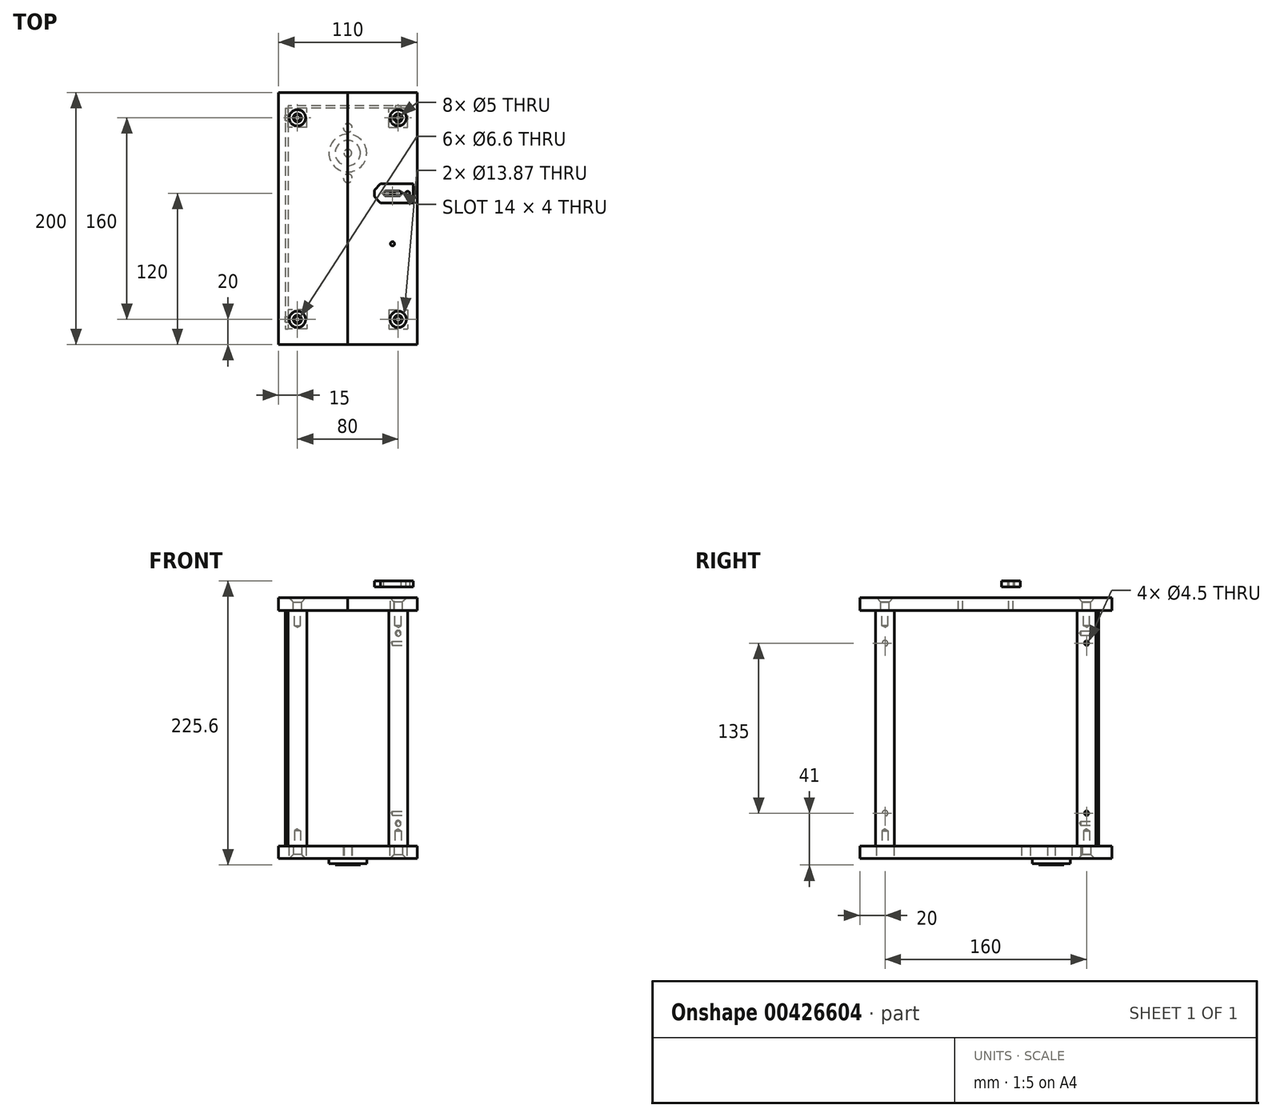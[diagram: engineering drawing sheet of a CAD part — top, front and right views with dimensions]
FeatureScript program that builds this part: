
annotation { "Feature Type Name" : "Feature", "Feature Type Description" : "" }
export const myFeature = defineFeature(function(context is Context, id is Id, definition is map)
    precondition{}
    {
        {
            var Q0;
            Q0=qCreatedBy(makeId("Top.planeOp"),FACE);
            cPlane(context, id + "F0", {"entities" : qUnion([Q0]), "cplaneType" : CPlaneType.OFFSET, "offset" : 197 * mm, "width" : 150 * mm, "height" : 150 * mm});
        }
        {
            var Q0;
            Q0=qCreatedBy(makeId("Front.planeOp"),FACE);
            var sketch = newSketch(context, id + "F1", { "sketchPlane" : qUnion([Q0])});
            skLineSegment(sketch, "E0", {"start": v(0, 0) * mm, "end": v(0, 306.43) * mm});
            skSolve(sketch);
        }
        {
            var Q0;
            Q0=qCreatedBy(makeId("Top.planeOp"),FACE);
            var sketch = newSketch(context, id + "F2", { "sketchPlane" : qUnion([Q0])});
            skCircle(sketch, "E1", {"center": v(0, 20) * mm, "radius": 3.5 * mm});
            skCircle(sketch, "E2.MirrorC", {"center": v(0, -20) * mm, "radius": 3.5 * mm});
            skPoint(sketch, "E3", {"position": v(0, 0) * mm});
            skSolve(sketch);
        }
        {
            var Q0;
            Q0=qCreatedBy(makeId("Top.planeOp"),FACE);
            var sketch = newSketch(context, id + "F3", { "sketchPlane" : qUnion([Q0])});
            skLineSegment(sketch, "E4.bottom", {"start": v(0, 48) * mm, "end": v(55, 48) * mm});
            skLineSegment(sketch, "E4.top", {"start": v(0, -152) * mm, "end": v(55, -152) * mm});
            skLineSegment(sketch, "E4.left", {"start": v(0, 48) * mm, "end": v(0, -152) * mm});
            skLineSegment(sketch, "E4.right", {"start": v(55, 48) * mm, "end": v(55, -152) * mm});
            skCircle(sketch, "E5", {"center": v(40, 28) * mm, "radius": 6.93 * mm});
            skLineSegment(sketch, "E6", {"start": v(55, -52) * mm, "end": v(0, -52) * mm, "construction": true});
            skCircle(sketch, "E7.MirrorC", {"center": v(40, -132) * mm, "radius": 6.93 * mm});
            skSolve(sketch);
        }
        {
            var Q0;
            Q0=sQuery(id+"F3.wireOp",VERTEX,"E4.right.start");
            var Q1;
            Q1=sQuery(id+"F3.wireOp",VERTEX,"E4.right.end");
            cPlane(context, id + "F4", {"entities" : qUnion([Q0, Q1]), "cplaneType" : CPlaneType.MID_PLANE, "offset" : 25 * mm, "width" : 150 * mm, "height" : 150 * mm});
        }
        {
            var Q0;
            Q0=makeQuery(id+"F3.imprint","IMPRINT",FACE,{"disambiguationData":[TD([[makeQuery(id+"F3.imprint","IMPRINT",EDGE,{"derivedFrom":sQuery(id+"F3.wireOp",EDGE,"E4.bottom")}),-1.0]])]});
            var Q1;
            Q1=makeQuery(id+"F3.imprint","IMPRINT",FACE,{"disambiguationData":[TD([[makeQuery(id+"F3.imprint","IMPRINT",EDGE,{"derivedFrom":sQuery(id+"F3.wireOp",EDGE,"E7.MirrorC")}),-1.0]])]});
            var Q2;
            Q2=makeQuery(id+"F3.imprint","IMPRINT",FACE,{"disambiguationData":[TD([[makeQuery(id+"F3.imprint","IMPRINT",EDGE,{"derivedFrom":sQuery(id+"F3.wireOp",EDGE,"E5")}),1.0]])]});
            extrude(context, id + "F5", {"entities" : qUnion([Q0, Q1, Q2]), "depth" : 10 * mm});
        }
        {
            var Q0;
            Q0=sQuery(id+"F3.wireOp",VERTEX,"E5.center");
            var Q1;
            Q1=sQuery(id+"F3.wireOp",VERTEX,"E7.MirrorC.center");
            var Q2;
            Q2=makeQuery(id+"F5.opExtrude","SWEPT_BODY",BODY,{"disambiguationData":[OSD([sQuery(id+"F3.wireOp",EDGE,"E4.bottom"),sQuery(id+"F3.wireOp",EDGE,"E4.top"),sQuery(id+"F3.wireOp",EDGE,"E4.left"),sQuery(id+"F3.wireOp",EDGE,"E4.right")])]});
            hole(context, id + "F6", {"style" : HoleStyle.C_SINK, "endStyle" : HoleEndStyle.THROUGH, "oppositeDirection" : true, "holeDiameter" : 6.6 * mm, "cSinkDiameter" : 13 * mm, "cSinkAngle" : 90 * degree, "isTappedThrough" : true, "tappedDepth" : 12 * mm, "tapClearance" : 3, "locations" : qUnion([Q0, Q1]), "scope" : qUnion([Q2])});
        }
        {
            var Q0;
            Q0=makeQuery(id+"F5.opExtrude","SWEPT_BODY",BODY,{"disambiguationData":[OSD([sQuery(id+"F3.wireOp",EDGE,"E4.bottom"),sQuery(id+"F3.wireOp",EDGE,"E4.top"),sQuery(id+"F3.wireOp",EDGE,"E4.left"),sQuery(id+"F3.wireOp",EDGE,"E4.right")])]});
            var Q1;
            Q1=qCreatedBy(makeId("Right.planeOp"),FACE);
            mirror(context, id + "F7", {"operationType" : NewBodyOperationType.ADD, "entities" : qUnion([Q0]), "mirrorPlane" : qUnion([Q1])});
        }
        {
            var Q0;
            Q0=qCreatedBy(id+"F0.planeOp",FACE);
            var sketch = newSketch(context, id + "F8", { "sketchPlane" : qUnion([Q0])});
            skLineSegment(sketch, "E8.bottom", {"start": v(0, 48) * mm, "end": v(55, 48) * mm});
            skLineSegment(sketch, "E8.top", {"start": v(0, -152) * mm, "end": v(55, -152) * mm});
            skLineSegment(sketch, "E8.left", {"start": v(0, 48) * mm, "end": v(0, -152) * mm});
            skLineSegment(sketch, "E8.right", {"start": v(55, 48) * mm, "end": v(55, -152) * mm});
            skSolve(sketch);
        }
        {
            var Q0;
            Q0 = qSketchRegion(id + "F8", true);
            extrude(context, id + "F9", {"entities" : qUnion([Q0]), "depth" : 10 * mm});
        }
        {
            var Q0;
            Q0=makeQuery(id+"F9.opExtrude","CAP_FACE",FACE,{"disambiguationData":[OSD([sQuery(id+"F8.wireOp",EDGE,"E8.bottom"),sQuery(id+"F8.wireOp",EDGE,"E8.top"),sQuery(id+"F8.wireOp",EDGE,"E8.left"),sQuery(id+"F8.wireOp",EDGE,"E8.right")])],"isStart":false});
            var sketch = newSketch(context, id + "F10", { "sketchPlane" : qUnion([Q0])});
            skPoint(sketch, "E9", {"position": v(40, 28) * mm});
            skPoint(sketch, "E10", {"position": v(40, -132) * mm});
            skSolve(sketch);
        }
        {
            var Q0;
            Q0=sQuery(id+"F10.wireOp",VERTEX,"E9");
            var Q1;
            Q1=sQuery(id+"F10.wireOp",VERTEX,"E10");
            var Q2;
            Q2=makeQuery(id+"F9.opExtrude","SWEPT_BODY",BODY,{"disambiguationData":[OSD([sQuery(id+"F8.wireOp",EDGE,"E8.bottom"),sQuery(id+"F8.wireOp",EDGE,"E8.top"),sQuery(id+"F8.wireOp",EDGE,"E8.left"),sQuery(id+"F8.wireOp",EDGE,"E8.right")])]});
            hole(context, id + "F11", {"style" : HoleStyle.C_SINK, "endStyle" : HoleEndStyle.THROUGH, "holeDiameter" : 6.6 * mm, "cSinkDiameter" : 13 * mm, "cSinkAngle" : 90 * degree, "isTappedThrough" : true, "tappedDepth" : 12 * mm, "tapClearance" : 3, "locations" : qUnion([Q0, Q1]), "scope" : qUnion([Q2])});
        }
        {
            var Q0;
            Q0=makeQuery(id+"F9.opExtrude","SWEPT_BODY",BODY,{"disambiguationData":[OSD([sQuery(id+"F8.wireOp",EDGE,"E8.bottom"),sQuery(id+"F8.wireOp",EDGE,"E8.top"),sQuery(id+"F8.wireOp",EDGE,"E8.left"),sQuery(id+"F8.wireOp",EDGE,"E8.right")])]});
            var Q1;
            Q1=qCreatedBy(makeId("Right.planeOp"),FACE);
            mirror(context, id + "F12", {"operationType" : NewBodyOperationType.ADD, "entities" : qUnion([Q0]), "mirrorPlane" : qUnion([Q1])});
        }
        {
            var Q0;
            {var subQ0=makeQuery(id+"F5.opExtrude","CAP_FACE",FACE,{"disambiguationData":[OSD([sQuery(id+"F3.wireOp",EDGE,"E4.bottom"),sQuery(id+"F3.wireOp",EDGE,"E4.top"),sQuery(id+"F3.wireOp",EDGE,"E4.left"),sQuery(id+"F3.wireOp",EDGE,"E4.right")])],"isStart":false});Q0=makeQuery(id+"F7.boolean.opBoolean","MERGE",FACE,{"derivedFrom":[subQ0,makeQuery(id+"F7.opPattern","COPY",FACE,{"derivedFrom":subQ0,"instanceName":"1"})]});}
            var sketch = newSketch(context, id + "F13", { "sketchPlane" : qUnion([Q0])});
            skLineSegment(sketch, "E11.bottom", {"start": v(32.5, 20.5) * mm, "end": v(47.5, 20.5) * mm});
            skLineSegment(sketch, "E11.top", {"start": v(32.5, 35.5) * mm, "end": v(47.5, 35.5) * mm});
            skLineSegment(sketch, "E11.left", {"start": v(32.5, 20.5) * mm, "end": v(32.5, 35.5) * mm});
            skLineSegment(sketch, "E11.right", {"start": v(47.5, 20.5) * mm, "end": v(47.5, 35.5) * mm});
            skPoint(sketch, "E11.middle", {"position": v(40, 28) * mm});
            skSolve(sketch);
        }
        {
            var Q0;
            Q0 = qSketchRegion(id + "F13", true);
            var Q1;
            Q1=qCreatedBy(id+"F0.planeOp",FACE);
            extrude(context, id + "F14", {"entities" : qUnion([Q0]), "endBound" : BoundingType.UP_TO_SURFACE, "endBoundEntityFace" : qUnion([Q1]), "depth" : 25 * mm});
        }
        {
            var Q0;
            Q0=sQuery(id+"F3.wireOp",VERTEX,"E5.center");
            var Q1;
            Q1=makeQuery(id+"F14.opExtrude","SWEPT_BODY",BODY,{"disambiguationData":[OSD([sQuery(id+"F13.wireOp",EDGE,"E11.bottom"),sQuery(id+"F13.wireOp",EDGE,"E11.top"),sQuery(id+"F13.wireOp",EDGE,"E11.left"),sQuery(id+"F13.wireOp",EDGE,"E11.right")])]});
            hole(context, id + "F15", {"style" : HoleStyle.SIMPLE, "endStyle" : HoleEndStyle.BLIND, "oppositeDirection" : true, "standardTappedOrClearance" : lookupTablePath({ "standard" : "ISO", "engagement" : "75%", "pitch" : "1 mm", "size" : "M6", "type" : "Tapped" }), "standardBlindInLast" : lookupTablePath({ "standard" : "ISO", "engagement" : "75%", "pitch" : "1 mm", "size" : "M6", "type" : "Tapped" }), "holeDiameter" : 5 * mm, "showTappedDepth" : true, "holeDepth" : 12 * mm, "isTappedThrough" : true, "tappedDepth" : 9 * mm, "tapClearance" : 3, "locations" : qUnion([Q0]), "scope" : qUnion([Q1]), "majorDiameter" : 6 * mm});
        }
        {
            var Q0;
            Q0=sQuery(id+"F10.wireOp",VERTEX,"E9");
            var Q1;
            Q1=makeQuery(id+"F14.opExtrude","SWEPT_BODY",BODY,{"disambiguationData":[OSD([sQuery(id+"F13.wireOp",EDGE,"E11.bottom"),sQuery(id+"F13.wireOp",EDGE,"E11.top"),sQuery(id+"F13.wireOp",EDGE,"E11.left"),sQuery(id+"F13.wireOp",EDGE,"E11.right")])]});
            hole(context, id + "F16", {"style" : HoleStyle.SIMPLE, "endStyle" : HoleEndStyle.BLIND, "standardTappedOrClearance" : lookupTablePath({ "standard" : "ISO", "engagement" : "75%", "pitch" : "1 mm", "size" : "M6", "type" : "Tapped" }), "standardBlindInLast" : lookupTablePath({ "standard" : "ISO", "engagement" : "75%", "pitch" : "1 mm", "size" : "M6", "type" : "Tapped" }), "holeDiameter" : 5 * mm, "showTappedDepth" : true, "holeDepth" : 12 * mm, "isTappedThrough" : true, "tappedDepth" : 9 * mm, "tapClearance" : 3, "locations" : qUnion([Q0]), "scope" : qUnion([Q1]), "majorDiameter" : 6 * mm});
        }
        {
            var Q0;
            Q0=makeQuery(id+"F14.opExtrude","SWEPT_BODY",BODY,{"disambiguationData":[OSD([sQuery(id+"F13.wireOp",EDGE,"E11.bottom"),sQuery(id+"F13.wireOp",EDGE,"E11.top"),sQuery(id+"F13.wireOp",EDGE,"E11.left"),sQuery(id+"F13.wireOp",EDGE,"E11.right")])]});
            var Q1;
            Q1=qCreatedBy(id+"F4.planeOp",FACE);
            mirror(context, id + "F17", {"entities" : qUnion([Q0]), "mirrorPlane" : qUnion([Q1])});
        }
        {
            var Q0;
            Q0=makeQuery(id+"F17.opPattern","COPY",BODY,{"derivedFrom":makeQuery(id+"F14.opExtrude","SWEPT_BODY",BODY,{"disambiguationData":[OSD([sQuery(id+"F13.wireOp",EDGE,"E11.bottom"),sQuery(id+"F13.wireOp",EDGE,"E11.top"),sQuery(id+"F13.wireOp",EDGE,"E11.left"),sQuery(id+"F13.wireOp",EDGE,"E11.right")])]}),"instanceName":"1"});
            var Q1;
            Q1=makeQuery(id+"F14.opExtrude","SWEPT_BODY",BODY,{"disambiguationData":[OSD([sQuery(id+"F13.wireOp",EDGE,"E11.bottom"),sQuery(id+"F13.wireOp",EDGE,"E11.top"),sQuery(id+"F13.wireOp",EDGE,"E11.left"),sQuery(id+"F13.wireOp",EDGE,"E11.right")])]});
            var Q2;
            Q2=qCreatedBy(makeId("Right.planeOp"),FACE);
            mirror(context, id + "F18", {"entities" : qUnion([Q0, Q1]), "mirrorPlane" : qUnion([Q2])});
        }
        {
            var Q0;
            Q0=sQuery(id+"F2.wireOp",VERTEX,"E1.center");
            var Q1;
            Q1=sQuery(id+"F2.wireOp",VERTEX,"E2.MirrorC.center");
            var Q2;
            Q2=makeQuery(id+"F5.opExtrude","SWEPT_BODY",BODY,{"disambiguationData":[OSD([sQuery(id+"F3.wireOp",EDGE,"E4.bottom"),sQuery(id+"F3.wireOp",EDGE,"E4.top"),sQuery(id+"F3.wireOp",EDGE,"E4.left"),sQuery(id+"F3.wireOp",EDGE,"E4.right")])]});
            hole(context, id + "F19", {"style" : HoleStyle.SIMPLE, "endStyle" : HoleEndStyle.THROUGH, "oppositeDirection" : true, "holeDiameter" : 7 * mm, "isTappedThrough" : true, "tappedDepth" : 12 * mm, "tapClearance" : 3, "locations" : qUnion([Q0, Q1]), "scope" : qUnion([Q2])});
        }
        {
            var Q0;
            Q0=sQuery(id+"F2.wireOp",VERTEX,"E3");
            var Q1;
            Q1=makeQuery(id+"F5.opExtrude","SWEPT_BODY",BODY,{"disambiguationData":[OSD([sQuery(id+"F3.wireOp",EDGE,"E4.bottom"),sQuery(id+"F3.wireOp",EDGE,"E4.top"),sQuery(id+"F3.wireOp",EDGE,"E4.left"),sQuery(id+"F3.wireOp",EDGE,"E4.right")])]});
            hole(context, id + "F20", {"style" : HoleStyle.SIMPLE, "endStyle" : HoleEndStyle.THROUGH, "oppositeDirection" : true, "holeDiameter" : 6 * mm, "majorDiameter" : 8 * mm, "isTappedThrough" : true, "tappedDepth" : 8 * mm, "tapClearance" : 3, "startFromSketch" : true, "locations" : qUnion([Q0]), "scope" : qUnion([Q1])});
        }
        {
            var Q0;
            Q0=makeQuery(id+"F10.imprint","IMPRINT",FACE,{"disambiguationData":[TD([[makeQuery(id+"F10.imprint","IMPRINT",EDGE,{"derivedFrom":makeQuery(id+"F9.opExtrude","CAP_EDGE",EDGE,{"disambiguationData":[OSD([sQuery(id+"F8.wireOp",EDGE,"E8.bottom")])],"isStart":false})}),-1.0]])]});
            var sketch = newSketch(context, id + "F21", { "sketchPlane" : qUnion([Q0])});
            skLineSegment(sketch, "E12", {"start": v(39.5, 0) * mm, "end": v(39.5, -47) * mm, "construction": true});
            skArc(sketch, "E13.0.startCap", {"start": v(37, -17) * mm, "mid": v(39.5, -14.5) * mm, "end": v(42, -17) * mm});
            skArc(sketch, "E13.0.endCap", {"start": v(42, -47) * mm, "mid": v(39.5, -49.5) * mm, "end": v(37, -47) * mm});
            skLineSegment(sketch, "E13.0.left", {"start": v(42, -17) * mm, "end": v(42, -47) * mm});
            skLineSegment(sketch, "E13.0.right", {"start": v(37, -17) * mm, "end": v(37, -47) * mm});
            skLineSegment(sketch, "E14", {"start": v(14.12, -32) * mm, "end": v(52, -32) * mm, "construction": true});
            skArc(sketch, "E15.MirrorCS", {"start": v(-37, -17) * mm, "mid": v(-39.5, -14.5) * mm, "end": v(-42, -17) * mm});
            skArc(sketch, "E16.MirrorCS", {"start": v(-42, -47) * mm, "mid": v(-39.5, -49.5) * mm, "end": v(-37, -47) * mm});
            skLineSegment(sketch, "E17.MirrorCS", {"start": v(-37, -17) * mm, "end": v(-37, -47) * mm});
            skLineSegment(sketch, "E18.MirrorCS", {"start": v(-14.12, -32) * mm, "end": v(-52, -32) * mm, "construction": true});
            skLineSegment(sketch, "E19.MirrorCS", {"start": v(-39.5, 0) * mm, "end": v(-39.5, -47) * mm, "construction": true});
            skLineSegment(sketch, "E20.MirrorCS", {"start": v(-42, -17) * mm, "end": v(-42, -47) * mm});
            skSolve(sketch);
        }
        {
            var Q0;
            Q0=makeQuery(id+"F14.opExtrude","SWEPT_FACE",FACE,{"disambiguationData":[OSD([sQuery(id+"F13.wireOp",EDGE,"E11.top")])]});
            var sketch = newSketch(context, id + "F22", { "sketchPlane" : qUnion([Q0])});
            skLineSegment(sketch, "E21.bottom", {"start": v(-47.5, 10) * mm, "end": v(47.5, 10) * mm});
            skLineSegment(sketch, "E21.top", {"start": v(-47.5, 197) * mm, "end": v(47.5, 197) * mm});
            skLineSegment(sketch, "E21.left", {"start": v(-47.5, 10) * mm, "end": v(-47.5, 197) * mm});
            skLineSegment(sketch, "E21.right", {"start": v(47.5, 10) * mm, "end": v(47.5, 197) * mm});
            skSolve(sketch);
        }
        {
            var Q0;
            Q0 = qSketchRegion(id + "F22", true);
            extrude(context, id + "F23", {"entities" : qUnion([Q0]), "depth" : 2 * mm});
        }
        {
            var Q0;
            Q0=makeQuery(id+"F14.opExtrude","SWEPT_FACE",FACE,{"disambiguationData":[OSD([sQuery(id+"F13.wireOp",EDGE,"E11.top")])]});
            var sketch = newSketch(context, id + "F24", { "sketchPlane" : qUnion([Q0])});
            skPoint(sketch, "E22", {"position": v(-40, 179) * mm});
            skPoint(sketch, "E23", {"position": v(-40, 28) * mm});
            skLineSegment(sketch, "E24", {"start": v(-40, 179) * mm, "end": v(-40, 28) * mm, "construction": true});
            skLineSegment(sketch, "E25", {"start": v(-53.3, 103.5) * mm, "end": v(-21, 103.5) * mm, "construction": true});
            skSolve(sketch);
        }
        {
            var Q0;
            Q0=makeQuery(id+"F14.opExtrude","SWEPT_FACE",FACE,{"disambiguationData":[OSD([sQuery(id+"F13.wireOp",EDGE,"E11.right")])]});
            var sketch = newSketch(context, id + "F25", { "sketchPlane" : qUnion([Q0])});
            skLineSegment(sketch, "E26", {"start": v(28, 166.6) * mm, "end": v(28, 36.55) * mm, "construction": true});
            skPoint(sketch, "E27", {"position": v(28, 171) * mm});
            skPoint(sketch, "E28", {"position": v(28, 36) * mm});
            skLineSegment(sketch, "E29", {"start": v(-12.44, 103.5) * mm, "end": v(67.72, 103.5) * mm, "construction": true});
            skPoint(sketch, "E30.MirrorP", {"position": v(-132, 171) * mm});
            skPoint(sketch, "E31.MirrorP", {"position": v(-132, 36) * mm});
            skSolve(sketch);
        }
        {
            var Q0;
            Q0=sQuery(id+"F24.wireOp",VERTEX,"E22");
            var Q1;
            Q1=sQuery(id+"F24.wireOp",VERTEX,"E23");
            var Q2;
            Q2=makeQuery(id+"F14.opExtrude","SWEPT_BODY",BODY,{"disambiguationData":[OSD([sQuery(id+"F13.wireOp",EDGE,"E11.bottom"),sQuery(id+"F13.wireOp",EDGE,"E11.top"),sQuery(id+"F13.wireOp",EDGE,"E11.left"),sQuery(id+"F13.wireOp",EDGE,"E11.right")])]});
            hole(context, id + "F26", {"style" : HoleStyle.SIMPLE, "endStyle" : HoleEndStyle.BLIND, "standardTappedOrClearance" : lookupTablePath({ "standard" : "ISO", "engagement" : "75%", "pitch" : "0.7 mm", "size" : "M4", "type" : "Tapped" }), "standardBlindInLast" : lookupTablePath({ "standard" : "ISO", "engagement" : "75%", "pitch" : "0.7 mm", "size" : "M4", "type" : "Tapped" }), "holeDiameter" : 3.3 * mm, "showTappedDepth" : true, "holeDepth" : 12 * mm, "isTappedThrough" : true, "tappedDepth" : 9.9 * mm, "tapClearance" : 3, "locations" : qUnion([Q0, Q1]), "scope" : qUnion([Q2]), "majorDiameter" : 4 * mm});
        }
        {
            var Q0;
            Q0=sQuery(id+"F25.wireOp",VERTEX,"E27");
            var Q1;
            Q1=sQuery(id+"F25.wireOp",VERTEX,"E28");
            var Q2;
            Q2=makeQuery(id+"F14.opExtrude","SWEPT_BODY",BODY,{"disambiguationData":[OSD([sQuery(id+"F13.wireOp",EDGE,"E11.bottom"),sQuery(id+"F13.wireOp",EDGE,"E11.top"),sQuery(id+"F13.wireOp",EDGE,"E11.left"),sQuery(id+"F13.wireOp",EDGE,"E11.right")])]});
            hole(context, id + "F27", {"style" : HoleStyle.SIMPLE, "endStyle" : HoleEndStyle.BLIND, "standardTappedOrClearance" : lookupTablePath({ "standard" : "ISO", "engagement" : "75%", "pitch" : "0.7 mm", "size" : "M4", "type" : "Tapped" }), "standardBlindInLast" : lookupTablePath({ "standard" : "ISO", "engagement" : "75%", "pitch" : "0.7 mm", "size" : "M4", "type" : "Tapped" }), "holeDiameter" : 3.3 * mm, "showTappedDepth" : true, "holeDepth" : 12 * mm, "isTappedThrough" : true, "tappedDepth" : 9.9 * mm, "tapClearance" : 3, "locations" : qUnion([Q0, Q1]), "scope" : qUnion([Q2]), "majorDiameter" : 4 * mm});
        }
        {
            var Q0;
            Q0=sQuery(id+"F24.wireOp",VERTEX,"E22");
            var Q1;
            Q1=sQuery(id+"F24.wireOp",VERTEX,"E23");
            var Q2;
            Q2=makeQuery(id+"F23.opExtrude","SWEPT_BODY",BODY,{"disambiguationData":[OSD([sQuery(id+"F22.wireOp",EDGE,"E21.bottom"),sQuery(id+"F22.wireOp",EDGE,"E21.top"),sQuery(id+"F22.wireOp",EDGE,"E21.left"),sQuery(id+"F22.wireOp",EDGE,"E21.right")])]});
            hole(context, id + "F28", {"style" : HoleStyle.SIMPLE, "endStyle" : HoleEndStyle.THROUGH, "oppositeDirection" : true, "holeDiameter" : 4.5 * mm, "isTappedThrough" : true, "tappedDepth" : 9.9 * mm, "tapClearance" : 3, "locations" : qUnion([Q0, Q1]), "scope" : qUnion([Q2])});
        }
        {
            var Q0;
            Q0=qCreatedBy(id+"F0.planeOp",FACE);
            cPlane(context, id + "F29", {"entities" : qUnion([Q0]), "cplaneType" : CPlaneType.OFFSET, "offset" : 18.6 * mm, "width" : 150 * mm, "height" : 150 * mm});
        }
        {
            var Q0;
            Q0=qCreatedBy(id+"F29.planeOp",FACE);
            var sketch = newSketch(context, id + "F30", { "sketchPlane" : qUnion([Q0])});
            skLineSegment(sketch, "E32.bottom", {"start": v(21, -39.5) * mm, "end": v(52, -39.5) * mm});
            skLineSegment(sketch, "E32.top", {"start": v(21, -24.5) * mm, "end": v(52, -24.5) * mm});
            skLineSegment(sketch, "E32.left", {"start": v(21, -39.5) * mm, "end": v(21, -24.5) * mm});
            skLineSegment(sketch, "E32.right", {"start": v(52, -39.5) * mm, "end": v(52, -24.5) * mm});
            skLineSegment(sketch, "E33", {"start": v(25, -67.78) * mm, "end": v(25, -21.75) * mm, "construction": true});
            skLineSegment(sketch, "E34", {"start": v(52, -32) * mm, "end": v(21, -32) * mm, "construction": true});
            skPoint(sketch, "E35", {"position": v(30.5, -32) * mm});
            skPoint(sketch, "E36", {"position": v(47.5, -32) * mm});
            skPoint(sketch, "E37", {"position": v(40.5, -32) * mm});
            skPoint(sketch, "E38", {"position": v(35.5, -32) * mm});
            skLineSegment(sketch, "E39", {"start": v(35.5, -29.4) * mm, "end": v(35.5, -73.02) * mm, "construction": true});
            skCircle(sketch, "E40", {"center": v(30.5, -32) * mm, "radius": 3.5 * mm, "construction": true});
            skCircle(sketch, "E41", {"center": v(40.5, -32) * mm, "radius": 3.5 * mm, "construction": true});
            skCircle(sketch, "E42", {"center": v(47.5, -32) * mm, "radius": 2 * mm, "construction": true});
            skPoint(sketch, "E43", {"position": v(35.5, -72) * mm});
            skSolve(sketch);
        }
        {
            var Q0;
            Q0=makeQuery(id+"F30.imprint","IMPRINT",FACE,{"disambiguationData":[TD([[makeQuery(id+"F30.imprint","IMPRINT",EDGE,{"derivedFrom":sQuery(id+"F30.wireOp",EDGE,"E32.bottom")}),1.0]])]});
            extrude(context, id + "F31", {"entities" : qUnion([Q0]), "depth" : 5 * mm});
        }
        {
            var Q0;
            Q0=makeQuery(id+"F31.opExtrude","SWEPT_EDGE",EDGE,{"disambiguationData":[OSD([sQuery(id+"F30.wireOp",EDGE,"E32.bottom"),sQuery(id+"F30.wireOp",EDGE,"E32.left")])]});
            var Q1;
            Q1=makeQuery(id+"F31.opExtrude","SWEPT_EDGE",EDGE,{"disambiguationData":[OSD([sQuery(id+"F30.wireOp",EDGE,"E32.top"),sQuery(id+"F30.wireOp",EDGE,"E32.left")])]});
            chamfer(context, id + "F32", {"entities" : qUnion([Q0, Q1]), "width" : 5 * mm, "tangentPropagation" : true});
        }
        {
            var Q0;
            Q0=makeQuery(id+"F31.opExtrude","CAP_FACE",FACE,{"disambiguationData":[OSD([sQuery(id+"F30.wireOp",EDGE,"E32.bottom"),sQuery(id+"F30.wireOp",EDGE,"E32.top"),sQuery(id+"F30.wireOp",EDGE,"E32.left"),sQuery(id+"F30.wireOp",EDGE,"E32.right")])],"isStart":false});
            var sketch = newSketch(context, id + "F33", { "sketchPlane" : qUnion([Q0])});
            skLineSegment(sketch, "E44", {"start": v(30.5, -32) * mm, "end": v(40.5, -32) * mm, "construction": true});
            skArc(sketch, "E45.0.startCap", {"start": v(30.5, -34) * mm, "mid": v(28.5, -32) * mm, "end": v(30.5, -30) * mm});
            skArc(sketch, "E45.0.endCap", {"start": v(40.5, -30) * mm, "mid": v(42.5, -32) * mm, "end": v(40.5, -34) * mm});
            skLineSegment(sketch, "E45.0.left", {"start": v(30.5, -30) * mm, "end": v(40.5, -30) * mm});
            skLineSegment(sketch, "E45.0.right", {"start": v(30.5, -34) * mm, "end": v(40.5, -34) * mm});
            skSolve(sketch);
        }
        {
            var Q0;
            Q0 = qSketchRegion(id + "F33", true);
            extrude(context, id + "F34", {"entities" : qUnion([Q0]), "operationType" : NewBodyOperationType.REMOVE, "endBound" : BoundingType.UP_TO_NEXT, "oppositeDirection" : true, "depth" : 25 * mm});
        }
        {
            var Q0;
            Q0=sQuery(id+"F30.wireOp",VERTEX,"E36");
            var Q1;
            Q1=makeQuery(id+"F31.opExtrude","SWEPT_BODY",BODY,{"disambiguationData":[OSD([sQuery(id+"F30.wireOp",EDGE,"E32.bottom"),sQuery(id+"F30.wireOp",EDGE,"E32.top"),sQuery(id+"F30.wireOp",EDGE,"E32.left"),sQuery(id+"F30.wireOp",EDGE,"E32.right")])]});
            hole(context, id + "F35", {"style" : HoleStyle.SIMPLE, "endStyle" : HoleEndStyle.THROUGH, "oppositeDirection" : true, "standardTappedOrClearance" : lookupTablePath({ "standard" : "ISO", "engagement" : "75%", "pitch" : "0.7 mm", "size" : "M4", "type" : "Tapped" }), "standardBlindInLast" : lookupTablePath({ "standard" : "ISO", "engagement" : "75%", "pitch" : "0.7 mm", "size" : "M4", "type" : "Tapped" }), "holeDiameter" : 3.3 * mm, "showTappedDepth" : true, "isTappedThrough" : true, "tappedDepth" : 9.9 * mm, "tapClearance" : 3, "locations" : qUnion([Q0]), "scope" : qUnion([Q1]), "majorDiameter" : 4 * mm});
        }
        {
            var Q0;
            Q0=sQuery(id+"F30.wireOp",VERTEX,"E38");
            var Q1;
            Q1=sQuery(id+"F30.wireOp",VERTEX,"E43");
            var Q2;
            Q2=makeQuery(id+"F9.opExtrude","SWEPT_BODY",BODY,{"disambiguationData":[OSD([sQuery(id+"F8.wireOp",EDGE,"E8.bottom"),sQuery(id+"F8.wireOp",EDGE,"E8.top"),sQuery(id+"F8.wireOp",EDGE,"E8.left"),sQuery(id+"F8.wireOp",EDGE,"E8.right")])]});
            hole(context, id + "F36", {"style" : HoleStyle.SIMPLE, "endStyle" : HoleEndStyle.THROUGH, "standardTappedOrClearance" : lookupTablePath({ "standard" : "ISO", "engagement" : "75%", "pitch" : "0.7 mm", "size" : "M4", "type" : "Tapped" }), "standardBlindInLast" : lookupTablePath({ "standard" : "ISO", "engagement" : "75%", "pitch" : "0.7 mm", "size" : "M4", "type" : "Tapped" }), "holeDiameter" : 3.3 * mm, "showTappedDepth" : true, "isTappedThrough" : true, "tappedDepth" : 9.9 * mm, "tapClearance" : 3, "locations" : qUnion([Q0, Q1]), "scope" : qUnion([Q2]), "majorDiameter" : 4 * mm});
        }
        {
            var Q0;
            Q0=makeQuery(id+"F18.opPattern","COPY",FACE,{"derivedFrom":makeQuery(id+"F14.opExtrude","SWEPT_FACE",FACE,{"disambiguationData":[OSD([sQuery(id+"F13.wireOp",EDGE,"E11.right")])]}),"instanceName":"1"});
            var sketch = newSketch(context, id + "F37", { "sketchPlane" : qUnion([Q0])});
            skLineSegment(sketch, "E46.bottom", {"start": v(-35.5, 197) * mm, "end": v(139.5, 197) * mm});
            skLineSegment(sketch, "E46.top", {"start": v(-35.5, 10) * mm, "end": v(139.5, 10) * mm});
            skLineSegment(sketch, "E46.left", {"start": v(-35.5, 197) * mm, "end": v(-35.5, 10) * mm});
            skLineSegment(sketch, "E46.right", {"start": v(139.5, 197) * mm, "end": v(139.5, 10) * mm});
            skSolve(sketch);
        }
        {
            var Q0;
            Q0 = qSketchRegion(id + "F37", true);
            extrude(context, id + "F38", {"entities" : qUnion([Q0]), "depth" : 2 * mm});
        }
        {
            var Q0;
            Q0=sQuery(id+"F25.wireOp",VERTEX,"E30.MirrorP");
            var Q1;
            Q1=sQuery(id+"F25.wireOp",VERTEX,"E31.MirrorP");
            var Q2;
            Q2=sQuery(id+"F25.wireOp",VERTEX,"E28");
            var Q3;
            Q3=sQuery(id+"F25.wireOp",VERTEX,"E27");
            var Q4;
            Q4=makeQuery(id+"F38.opExtrude","SWEPT_BODY",BODY,{"disambiguationData":[OSD([sQuery(id+"F37.wireOp",EDGE,"E46.bottom"),sQuery(id+"F37.wireOp",EDGE,"E46.top"),sQuery(id+"F37.wireOp",EDGE,"E46.left"),sQuery(id+"F37.wireOp",EDGE,"E46.right")])]});
            hole(context, id + "F39", {"style" : HoleStyle.SIMPLE, "endStyle" : HoleEndStyle.THROUGH, "holeDiameter" : 4.5 * mm, "isTappedThrough" : true, "tappedDepth" : 9.9 * mm, "tapClearance" : 3, "locations" : qUnion([Q0, Q1, Q2, Q3]), "scope" : qUnion([Q4])});
        }
        {
            var Q0;
            {var subQ0=makeQuery(id+"F5.opExtrude","CAP_FACE",FACE,{"disambiguationData":[OSD([sQuery(id+"F3.wireOp",EDGE,"E4.bottom"),sQuery(id+"F3.wireOp",EDGE,"E4.top"),sQuery(id+"F3.wireOp",EDGE,"E4.left"),sQuery(id+"F3.wireOp",EDGE,"E4.right")])],"isStart":true});Q0=makeQuery(id+"F7.boolean.opBoolean","MERGE",FACE,{"derivedFrom":[subQ0,makeQuery(id+"F7.opPattern","COPY",FACE,{"derivedFrom":subQ0,"instanceName":"1"})]});}
            var sketch = newSketch(context, id + "F40", { "sketchPlane" : qUnion([Q0])});
            skCircle(sketch, "E47", {"center": v(0, 0) * mm, "radius": 15 * mm});
            skSolve(sketch);
        }
        {
            var Q0;
            Q0 = qSketchRegion(id + "F40", true);
            extrude(context, id + "F41", {"entities" : qUnion([Q0]), "depth" : 4 * mm, "offsetDistance" : 25 * mm});
        }
        {
            var Q0;
            Q0=makeQuery(id+"F41.opExtrude","CAP_FACE",FACE,{"disambiguationData":[OSD([sQuery(id+"F40.wireOp",EDGE,"E47")])],"isStart":false});
            var sketch = newSketch(context, id + "F42", { "sketchPlane" : qUnion([Q0])});
            skCircle(sketch, "E48", {"center": v(0, 0) * mm, "radius": 10 * mm});
            skSolve(sketch);
        }
        {
            var Q0;
            Q0=makeQuery(id+"F42.imprint","IMPRINT",FACE,{"disambiguationData":[TD([[makeQuery(id+"F42.imprint","IMPRINT",EDGE,{"derivedFrom":sQuery(id+"F42.wireOp",EDGE,"E48")}),1.0]])]});
            extrude(context, id + "F43", {"entities" : qUnion([Q0]), "operationType" : NewBodyOperationType.ADD, "depth" : 1 * mm, "offsetDistance" : 25 * mm});
        }
    });
